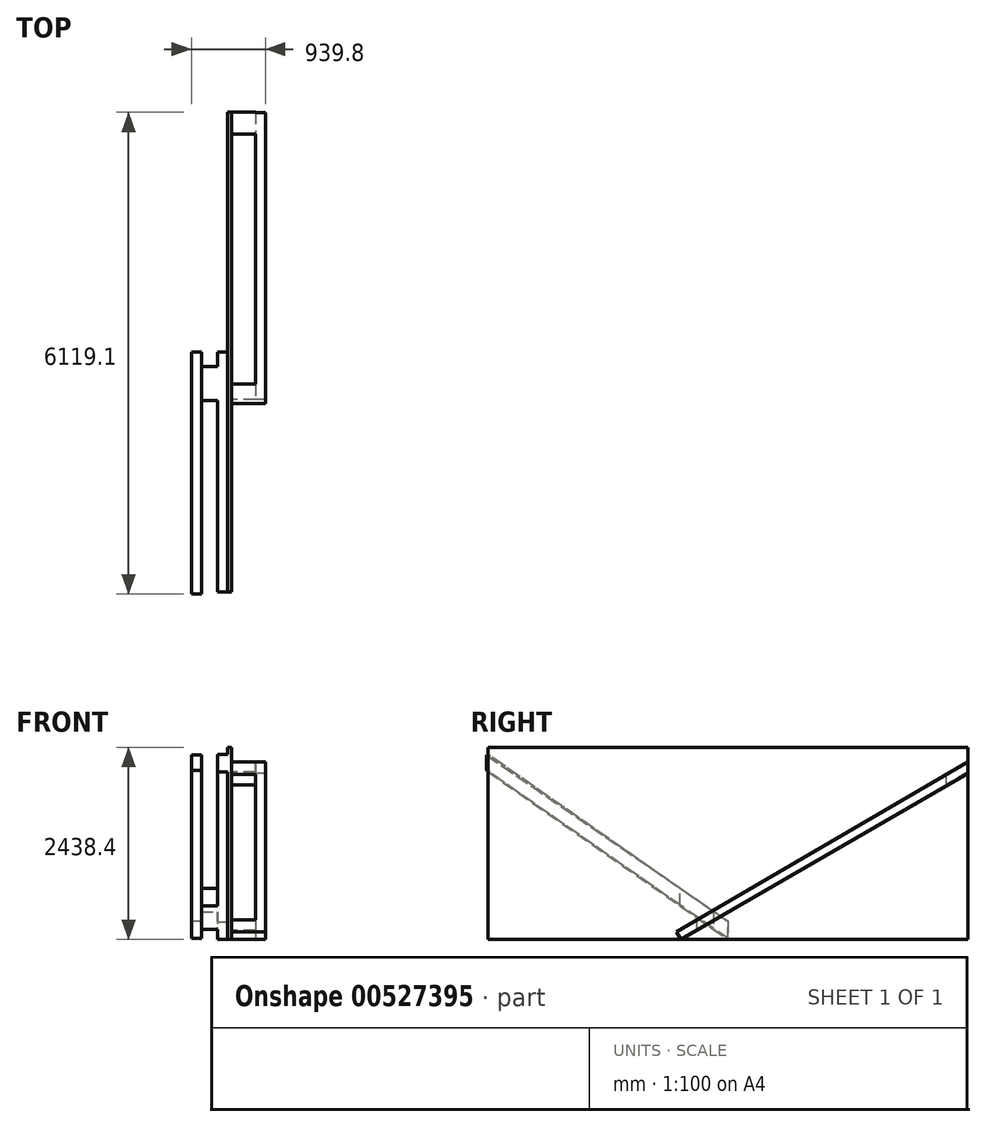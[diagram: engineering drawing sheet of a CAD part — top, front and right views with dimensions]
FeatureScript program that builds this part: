
annotation { "Feature Type Name" : "Feature", "Feature Type Description" : "" }
export const myFeature = defineFeature(function(context is Context, id is Id, definition is map)
    precondition{}
    {
        {
            var Q0;
            Q0=qCreatedBy(makeId("Right.planeOp"),FACE);
            var sketch = newSketch(context, id + "F0", { "sketchPlane" : qUnion([Q0])});
            skLineSegment(sketch, "E0.bottom", {"start": v(-3048, -1219.2) * mm, "end": v(3048, -1219.2) * mm});
            skLineSegment(sketch, "E0.top", {"start": v(-3048, 1219.2) * mm, "end": v(3048, 1219.2) * mm});
            skLineSegment(sketch, "E0.left", {"start": v(-3048, -1219.2) * mm, "end": v(-3048, 1219.2) * mm});
            skLineSegment(sketch, "E0.right", {"start": v(3048, -1219.2) * mm, "end": v(3048, 1219.2) * mm});
            skPoint(sketch, "E0.middle", {"position": v(0, 0) * mm});
            skSolve(sketch);
        }
        {
            var Q0;
            Q0=qSketchRegion(id+"F0",true);
            extrude(context, id + "F1", {"entities" : qUnion([Q0]), "depth" : 50.8 * mm});
        }
        {
            var Q0;
            Q0=makeQuery(id+"F1.opExtrude","CAP_FACE",FACE,{"disambiguationData":[OSD([sQuery(id+"F0.wireOp",EDGE,"E0.bottom"),sQuery(id+"F0.wireOp",EDGE,"E0.top"),sQuery(id+"F0.wireOp",EDGE,"E0.left"),sQuery(id+"F0.wireOp",EDGE,"E0.right")])],"isStart":false});
            var sketch = newSketch(context, id + "F2", { "sketchPlane" : qUnion([Q0])});
            skLineSegment(sketch, "E1", {"start": v(3048, 905.65) * mm, "end": v(2768.72, 742.92) * mm});
            skPoint(sketch, "E2", {"position": v(1224.66, -156.77) * mm});
            skLineSegment(sketch, "E3", {"start": v(-598.68, -1219.2) * mm, "end": v(-655.6, -1121.51) * mm});
            skLineSegment(sketch, "E4", {"start": v(-655.6, -1121.51) * mm, "end": v(-403.77, -974.77) * mm});
            skLineSegment(sketch, "E5", {"start": v(3048, 905.65) * mm, "end": v(3048, 1036.5) * mm});
            skLineSegment(sketch, "E6", {"start": v(-403.77, -974.77) * mm, "end": v(-403.77, -1105.63) * mm});
            skLineSegment(sketch, "E7", {"start": v(2768.72, 873.78) * mm, "end": v(2768.72, 742.92) * mm});
            skLineSegment(sketch, "E8.trimOffspring", {"start": v(2768.72, 873.78) * mm, "end": v(3048, 1036.5) * mm});
            skLineSegment(sketch, "E9.trimOffspring", {"start": v(-403.77, -1105.63) * mm, "end": v(-598.68, -1219.2) * mm});
            skSolve(sketch);
        }
        {
            var Q0;
            Q0=qSketchRegion(id+"F2",true);
            extrude(context, id + "F3", {"entities" : qUnion([Q0]), "operationType" : NewBodyOperationType.ADD, "depth" : 304.8 * mm});
        }
        {
            var Q0;
            Q0=makeQuery(id+"F1.opExtrude","CAP_FACE",FACE,{"disambiguationData":[OSD([sQuery(id+"F0.wireOp",EDGE,"E0.bottom"),sQuery(id+"F0.wireOp",EDGE,"E0.top"),sQuery(id+"F0.wireOp",EDGE,"E0.left"),sQuery(id+"F0.wireOp",EDGE,"E0.right")])],"isStart":true});
            var sketch = newSketch(context, id + "F4", { "sketchPlane" : qUnion([Q0])});
            skLineSegment(sketch, "E10", {"start": v(3048, 908.16) * mm, "end": v(0, -1219.2) * mm});
            skLineSegment(sketch, "E11", {"start": v(0, -1219.2) * mm, "end": v(0, -999.25) * mm});
            skLineSegment(sketch, "E12", {"start": v(0, -999.25) * mm, "end": v(3048, 1128.1) * mm});
            skLineSegment(sketch, "E13", {"start": v(3048, 1128.1) * mm, "end": v(3048, 908.16) * mm});
            skSolve(sketch);
        }
        {
            var Q0;
            Q0=makeQuery(id+"F4.imprint","IMPRINT",FACE,{"disambiguationData":[TD([[makeQuery(id+"F4.imprint","IMPRINT",EDGE,{"derivedFrom":sQuery(id+"F4.wireOp",EDGE,"E10")}),-1.0]])]});
            extrude(context, id + "F5", {"entities" : qUnion([Q0]), "operationType" : NewBodyOperationType.ADD, "depth" : 127 * mm});
        }
        {
            var Q0;
            Q0=makeQuery(id+"F5.opExtrude","CAP_FACE",FACE,{"disambiguationData":[OSD([sQuery(id+"F4.wireOp",EDGE,"E10"),sQuery(id+"F4.wireOp",EDGE,"E11"),sQuery(id+"F4.wireOp",EDGE,"E12"),sQuery(id+"F4.wireOp",EDGE,"E13")])],"isStart":false});
            var sketch = newSketch(context, id + "F6", { "sketchPlane" : qUnion([Q0])});
            skLineSegment(sketch, "E14", {"start": v(184.84, -870.25) * mm, "end": v(184.84, -1090.2) * mm});
            skLineSegment(sketch, "E15", {"start": v(184.84, -1090.2) * mm, "end": v(611.34, -792.51) * mm});
            skLineSegment(sketch, "E16", {"start": v(611.34, -792.51) * mm, "end": v(611.34, -572.56) * mm});
            skLineSegment(sketch, "E17", {"start": v(611.34, -572.56) * mm, "end": v(184.84, -870.25) * mm});
            skSolve(sketch);
        }
        {
            var Q0;
            Q0=makeQuery(id+"F6.imprint","IMPRINT",FACE,{"disambiguationData":[TD([[makeQuery(id+"F6.imprint","IMPRINT",EDGE,{"derivedFrom":sQuery(id+"F6.wireOp",EDGE,"E14")}),1.0]])]});
            extrude(context, id + "F7", {"entities" : qUnion([Q0]), "operationType" : NewBodyOperationType.ADD, "depth" : 203.2 * mm});
        }
        {
            var Q0;
            Q0=makeQuery(id+"F7.opExtrude","CAP_FACE",FACE,{"disambiguationData":[OSD([sQuery(id+"F6.wireOp",EDGE,"E14"),sQuery(id+"F6.wireOp",EDGE,"E15"),sQuery(id+"F6.wireOp",EDGE,"E16"),sQuery(id+"F6.wireOp",EDGE,"E17")])],"isStart":false});
            var sketch = newSketch(context, id + "F8", { "sketchPlane" : qUnion([Q0])});
            skSolve(sketch);
        }
        {
            var Q0;
            Q0=makeQuery(id+"F8.imprint","IMPRINT",FACE,{"disambiguationData":[TD([[makeQuery(id+"F8.imprint","IMPRINT",EDGE,{"derivedFrom":makeQuery(id+"F7.opExtrude","CAP_EDGE",EDGE,{"disambiguationData":[OSD([sQuery(id+"F6.wireOp",EDGE,"E14")])],"isStart":false})}),1.0]])]});
            var sketch = newSketch(context, id + "F9", { "sketchPlane" : qUnion([Q0])});
            skLineSegment(sketch, "E18", {"start": v(0, -1209.7) * mm, "end": v(3071.1, 929.14) * mm});
            skLineSegment(sketch, "E19", {"start": v(3071.1, 929.14) * mm, "end": v(3071.1, 1121.74) * mm});
            skLineSegment(sketch, "E20", {"start": v(3071.1, 1121.74) * mm, "end": v(0, -986.7) * mm});
            skLineSegment(sketch, "E21", {"start": v(0, -986.7) * mm, "end": v(0, -1209.7) * mm});
            skLineSegment(sketch, "E22", {"start": v(0, -1209.7) * mm, "end": v(0, -986.7) * mm});
            skSolve(sketch);
        }
        {
            var Q0;
            {var subQ5=makeQuery(id+"F8.imprint","IMPRINT",EDGE,{"derivedFrom":makeQuery(id+"F7.opExtrude","CAP_EDGE",EDGE,{"disambiguationData":[OSD([sQuery(id+"F6.wireOp",EDGE,"E17")])],"isStart":false})});Q0=makeQuery(id+"F9.imprint","IMPRINT",FACE,{"disambiguationData":[TD([[makeQuery(id+"F9.imprint","IMPRINT",EDGE,{"derivedFrom":subQ5}),-1.0]])]});}
            var Q1;
            {var subQ0=sQuery(id+"F9.wireOp",EDGE,"E19");Q1=makeQuery(id+"F9.imprint","IMPRINT",FACE,{"disambiguationData":[TD([[makeQuery(id+"F9.imprint","IMPRINT",EDGE,{"derivedFrom":subQ0}),1.0]])]});}
            extrude(context, id + "F10", {"entities" : qUnion([Q0, Q1]), "operationType" : NewBodyOperationType.ADD, "depth" : 127 * mm});
        }
        {
            var Q0;
            Q0=makeQuery(id+"F3.opExtrude","CAP_FACE",FACE,{"disambiguationData":[OSD([sQuery(id+"F2.wireOp",EDGE,"E3"),sQuery(id+"F2.wireOp",EDGE,"E4"),sQuery(id+"F2.wireOp",EDGE,"E6"),sQuery(id+"F2.wireOp",EDGE,"E9.trimOffspring")])],"isStart":false});
            var sketch = newSketch(context, id + "F11", { "sketchPlane" : qUnion([Q0])});
            skLineSegment(sketch, "E23", {"start": v(-655.6, -1121.51) * mm, "end": v(3045.2, 1034.87) * mm});
            skLineSegment(sketch, "E24", {"start": v(3045.2, 1034.87) * mm, "end": v(3045.2, 886.5) * mm});
            skLineSegment(sketch, "E25", {"start": v(3045.2, 886.5) * mm, "end": v(-598.68, -1219.2) * mm});
            skLineSegment(sketch, "E26", {"start": v(-598.68, -1219.2) * mm, "end": v(-655.6, -1121.51) * mm});
            skSolve(sketch);
        }
        {
            var Q0;
            Q0=qSketchRegion(id+"F11",true);
            extrude(context, id + "F12", {"entities" : qUnion([Q0]), "operationType" : NewBodyOperationType.ADD, "depth" : 127 * mm});
        }
    });
